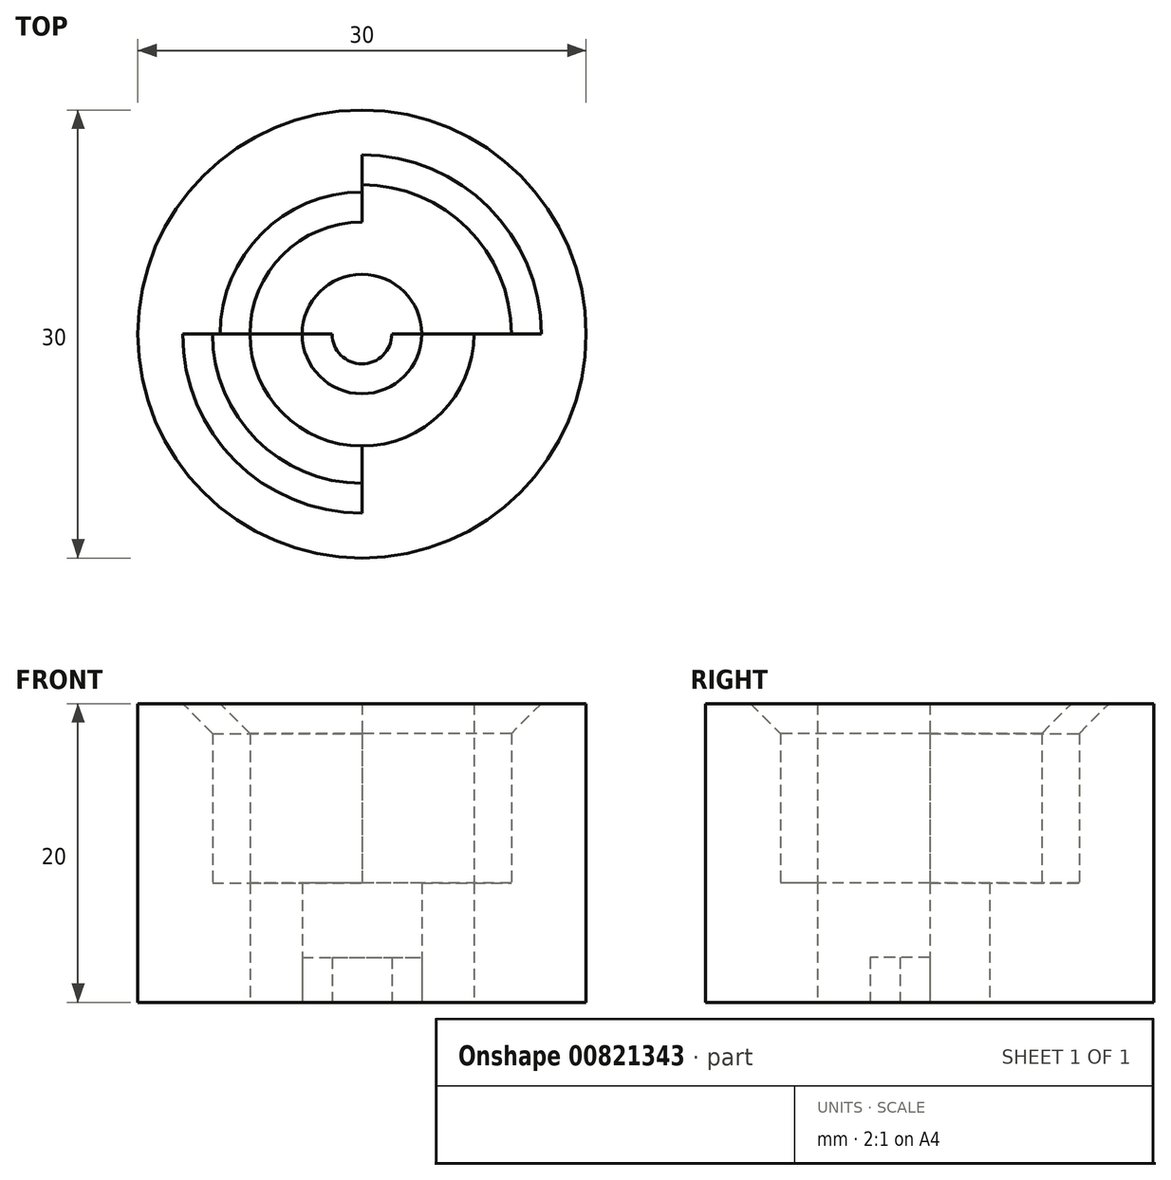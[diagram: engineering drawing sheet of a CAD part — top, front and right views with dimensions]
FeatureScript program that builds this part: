
annotation { "Feature Type Name" : "Feature", "Feature Type Description" : "" }
export const myFeature = defineFeature(function(context is Context, id is Id, definition is map)
    precondition{}
    {
        {
            var Q0;
            Q0=qCreatedBy(makeId("Top.planeOp"),FACE);
            var sketch = newSketch(context, id + "F0", { "sketchPlane" : qUnion([Q0])});
            skCircle(sketch, "E0", {"center": v(0, 0) * mm, "radius": 10 * mm});
            skCircle(sketch, "E1", {"center": v(0, 0) * mm, "radius": 7.5 * mm});
            skCircle(sketch, "E2", {"center": v(0, 0) * mm, "radius": 15 * mm});
            skCircle(sketch, "E3", {"center": v(0, 0) * mm, "radius": 2 * mm});
            skCircle(sketch, "E4", {"center": v(0, 0) * mm, "radius": 4 * mm});
            skLineSegment(sketch, "E5", {"start": v(0, 10) * mm, "end": v(0, -10) * mm});
            skLineSegment(sketch, "E6", {"start": v(-10, 0) * mm, "end": v(10, 0) * mm});
            skSolve(sketch);
        }
        {
            var Q0;
            {var subQ0=sQuery(id+"F0.wireOp",EDGE,"E5");var subQ1=sQuery(id+"F0.wireOp",EDGE,"E3");var subQ2=makeQuery(id+"F0.imprint","INTERSECT",VERTEX,{"disambiguationData":[OD(0.0)],"derivedFrom":[subQ1,subQ0]});Q0=makeQuery(id+"F0.imprint","IMPRINT",FACE,{"disambiguationData":[TD([[makeQuery(id+"F0.imprint","IMPRINT",EDGE,{"disambiguationData":[TD([[subQ2,1.0]])],"derivedFrom":subQ1}),-1.0]])]});}
            var Q1;
            {var subQ0=sQuery(id+"F0.wireOp",EDGE,"E5");var subQ1=sQuery(id+"F0.wireOp",EDGE,"E3");var subQ2=makeQuery(id+"F0.imprint","INTERSECT",VERTEX,{"disambiguationData":[OD(0.0)],"derivedFrom":[subQ1,subQ0]});Q1=makeQuery(id+"F0.imprint","IMPRINT",FACE,{"disambiguationData":[TD([[makeQuery(id+"F0.imprint","IMPRINT",EDGE,{"disambiguationData":[TD([[subQ2,-1.0]])],"derivedFrom":subQ1}),-1.0]])]});}
            var Q2;
            {var subQ0=sQuery(id+"F0.wireOp",EDGE,"E6");var subQ1=sQuery(id+"F0.wireOp",EDGE,"E3");var subQ2=makeQuery(id+"F0.imprint","INTERSECT",VERTEX,{"disambiguationData":[OD(1.0)],"derivedFrom":[subQ1,subQ0]});Q2=makeQuery(id+"F0.imprint","IMPRINT",FACE,{"disambiguationData":[TD([[makeQuery(id+"F0.imprint","IMPRINT",EDGE,{"disambiguationData":[TD([[subQ2,-1.0]])],"derivedFrom":subQ1}),-1.0]])]});}
            var Q3;
            {var subQ0=sQuery(id+"F0.wireOp",EDGE,"E6");var subQ1=sQuery(id+"F0.wireOp",EDGE,"E3");var subQ2=makeQuery(id+"F0.imprint","INTERSECT",VERTEX,{"disambiguationData":[OD(0.0)],"derivedFrom":[subQ1,subQ0]});Q3=makeQuery(id+"F0.imprint","IMPRINT",FACE,{"disambiguationData":[TD([[makeQuery(id+"F0.imprint","IMPRINT",EDGE,{"disambiguationData":[TD([[subQ2,1.0]])],"derivedFrom":subQ1}),-1.0]])]});}
            extrude(context, id + "F1", {"entities" : qUnion([Q0, Q1, Q2, Q3]), "depth" : 3 * mm, "offsetDistance" : 25 * mm});
        }
        {
            var Q0;
            {var subQ0=sQuery(id+"F0.wireOp",EDGE,"E5");var subQ1=sQuery(id+"F0.wireOp",EDGE,"E1");var subQ2=makeQuery(id+"F0.imprint","INTERSECT",VERTEX,{"disambiguationData":[OD(0.0)],"derivedFrom":[subQ1,subQ0]});Q0=makeQuery(id+"F0.imprint","IMPRINT",FACE,{"disambiguationData":[TD([[makeQuery(id+"F0.imprint","IMPRINT",EDGE,{"disambiguationData":[TD([[subQ2,1.0]])],"derivedFrom":subQ1}),1.0]])]});}
            var Q1;
            {var subQ0=sQuery(id+"F0.wireOp",EDGE,"E6");var subQ1=sQuery(id+"F0.wireOp",EDGE,"E1");var subQ2=makeQuery(id+"F0.imprint","INTERSECT",VERTEX,{"disambiguationData":[OD(1.0)],"derivedFrom":[subQ1,subQ0]});Q1=makeQuery(id+"F0.imprint","IMPRINT",FACE,{"disambiguationData":[TD([[makeQuery(id+"F0.imprint","IMPRINT",EDGE,{"disambiguationData":[TD([[subQ2,-1.0]])],"derivedFrom":subQ1}),1.0]])]});}
            var Q2;
            {var subQ0=sQuery(id+"F0.wireOp",EDGE,"E6");var subQ1=sQuery(id+"F0.wireOp",EDGE,"E1");var subQ2=makeQuery(id+"F0.imprint","INTERSECT",VERTEX,{"disambiguationData":[OD(0.0)],"derivedFrom":[subQ1,subQ0]});Q2=makeQuery(id+"F0.imprint","IMPRINT",FACE,{"disambiguationData":[TD([[makeQuery(id+"F0.imprint","IMPRINT",EDGE,{"disambiguationData":[TD([[subQ2,1.0]])],"derivedFrom":subQ1}),1.0]])]});}
            var Q3;
            {var subQ0=sQuery(id+"F0.wireOp",EDGE,"E5");var subQ1=sQuery(id+"F0.wireOp",EDGE,"E1");var subQ2=makeQuery(id+"F0.imprint","INTERSECT",VERTEX,{"disambiguationData":[OD(0.0)],"derivedFrom":[subQ1,subQ0]});Q3=makeQuery(id+"F0.imprint","IMPRINT",FACE,{"disambiguationData":[TD([[makeQuery(id+"F0.imprint","IMPRINT",EDGE,{"disambiguationData":[TD([[subQ2,-1.0]])],"derivedFrom":subQ1}),1.0]])]});}
            var Q4;
            {var subQ0=sQuery(id+"F0.wireOp",EDGE,"E5");var subQ1=sQuery(id+"F0.wireOp",EDGE,"E0");var subQ2=makeQuery(id+"F0.imprint","INTERSECT",VERTEX,{"disambiguationData":[OD(1.0)],"derivedFrom":[subQ1,subQ0]});Q4=makeQuery(id+"F0.imprint","IMPRINT",FACE,{"disambiguationData":[TD([[makeQuery(id+"F0.imprint","IMPRINT",EDGE,{"disambiguationData":[TD([[subQ2,1.0]])],"derivedFrom":subQ1}),1.0]])]});}
            var Q5;
            {var subQ0=sQuery(id+"F0.wireOp",EDGE,"E5");var subQ1=sQuery(id+"F0.wireOp",EDGE,"E0");var subQ2=makeQuery(id+"F0.imprint","INTERSECT",VERTEX,{"disambiguationData":[OD(0.0)],"derivedFrom":[subQ1,subQ0]});Q5=makeQuery(id+"F0.imprint","IMPRINT",FACE,{"disambiguationData":[TD([[makeQuery(id+"F0.imprint","IMPRINT",EDGE,{"disambiguationData":[TD([[subQ2,1.0]])],"derivedFrom":subQ1}),1.0]])]});}
            extrude(context, id + "F2", {"entities" : qUnion([Q0, Q1, Q2, Q3, Q4, Q5]), "operationType" : NewBodyOperationType.ADD, "depth" : 8 * mm, "offsetDistance" : 25 * mm});
        }
        {
            var Q0;
            {var subQ0=sQuery(id+"F0.wireOp",EDGE,"E5");var subQ1=sQuery(id+"F0.wireOp",EDGE,"E0");var subQ2=makeQuery(id+"F0.imprint","INTERSECT",VERTEX,{"disambiguationData":[OD(0.0)],"derivedFrom":[subQ1,subQ0]});Q0=makeQuery(id+"F0.imprint","IMPRINT",FACE,{"disambiguationData":[TD([[makeQuery(id+"F0.imprint","IMPRINT",EDGE,{"disambiguationData":[TD([[subQ2,-1.0]])],"derivedFrom":subQ1}),1.0]])]});}
            var Q1;
            {var subQ0=sQuery(id+"F0.wireOp",EDGE,"E5");var subQ1=sQuery(id+"F0.wireOp",EDGE,"E0");var subQ2=makeQuery(id+"F0.imprint","INTERSECT",VERTEX,{"disambiguationData":[OD(1.0)],"derivedFrom":[subQ1,subQ0]});Q1=makeQuery(id+"F0.imprint","IMPRINT",FACE,{"disambiguationData":[TD([[makeQuery(id+"F0.imprint","IMPRINT",EDGE,{"disambiguationData":[TD([[subQ2,-1.0]])],"derivedFrom":subQ1}),1.0]])]});}
            var Q2;
            Q2=makeQuery(id+"F0.imprint","IMPRINT",FACE,{"disambiguationData":[TD([[makeQuery(id+"F0.imprint","IMPRINT",EDGE,{"derivedFrom":sQuery(id+"F0.wireOp",EDGE,"E2")}),1.0]])]});
            extrude(context, id + "F3", {"entities" : qUnion([Q0, Q1, Q2]), "operationType" : NewBodyOperationType.ADD, "depth" : 20 * mm, "offsetDistance" : 25 * mm});
        }
        {
            var Q0;
            {var subQ0=sQuery(id+"F0.wireOp",EDGE,"E1");Q0=makeQuery(id+"F3.opExtrude","CAP_EDGE",EDGE,{"disambiguationData":[OSD([subQ0]),TDD([makeQuery(id+"F0.imprint","IMPRINT",EDGE,{"disambiguationData":[TD([[makeQuery(id+"F0.imprint","INTERSECT",VERTEX,{"disambiguationData":[OD(0.0)],"derivedFrom":[subQ0,sQuery(id+"F0.wireOp",EDGE,"E5")]}),-1.0]])],"derivedFrom":subQ0})])],"isStart":false});}
            var Q1;
            {var subQ0=sQuery(id+"F0.wireOp",EDGE,"E1");Q1=makeQuery(id+"F3.opExtrude","CAP_EDGE",EDGE,{"disambiguationData":[OSD([subQ0]),TDD([makeQuery(id+"F0.imprint","IMPRINT",EDGE,{"disambiguationData":[TD([[makeQuery(id+"F0.imprint","INTERSECT",VERTEX,{"disambiguationData":[OD(0.0)],"derivedFrom":[subQ0,sQuery(id+"F0.wireOp",EDGE,"E6")]}),1.0]])],"derivedFrom":subQ0})])],"isStart":false});}
            var Q2;
            {var subQ0=sQuery(id+"F0.wireOp",EDGE,"E0");Q2=makeQuery(id+"F3.opExtrude","CAP_EDGE",EDGE,{"disambiguationData":[OSD([subQ0]),TDD([makeQuery(id+"F0.imprint","IMPRINT",EDGE,{"disambiguationData":[TD([[makeQuery(id+"F0.imprint","INTERSECT",VERTEX,{"disambiguationData":[OD(0.0)],"derivedFrom":[subQ0,sQuery(id+"F0.wireOp",EDGE,"E5")]}),1.0]])],"derivedFrom":subQ0})])],"isStart":false});}
            var Q3;
            {var subQ0=sQuery(id+"F0.wireOp",EDGE,"E0");Q3=makeQuery(id+"F3.opExtrude","CAP_EDGE",EDGE,{"disambiguationData":[OSD([subQ0]),TDD([makeQuery(id+"F0.imprint","IMPRINT",EDGE,{"disambiguationData":[TD([[makeQuery(id+"F0.imprint","INTERSECT",VERTEX,{"disambiguationData":[OD(1.0)],"derivedFrom":[subQ0,sQuery(id+"F0.wireOp",EDGE,"E5")]}),1.0]])],"derivedFrom":subQ0})])],"isStart":false});}
            chamfer(context, id + "F4", {"entities" : qUnion([Q0, Q1, Q2, Q3]), "width" : 2 * mm, "tangentPropagation" : true});
        }
    });
